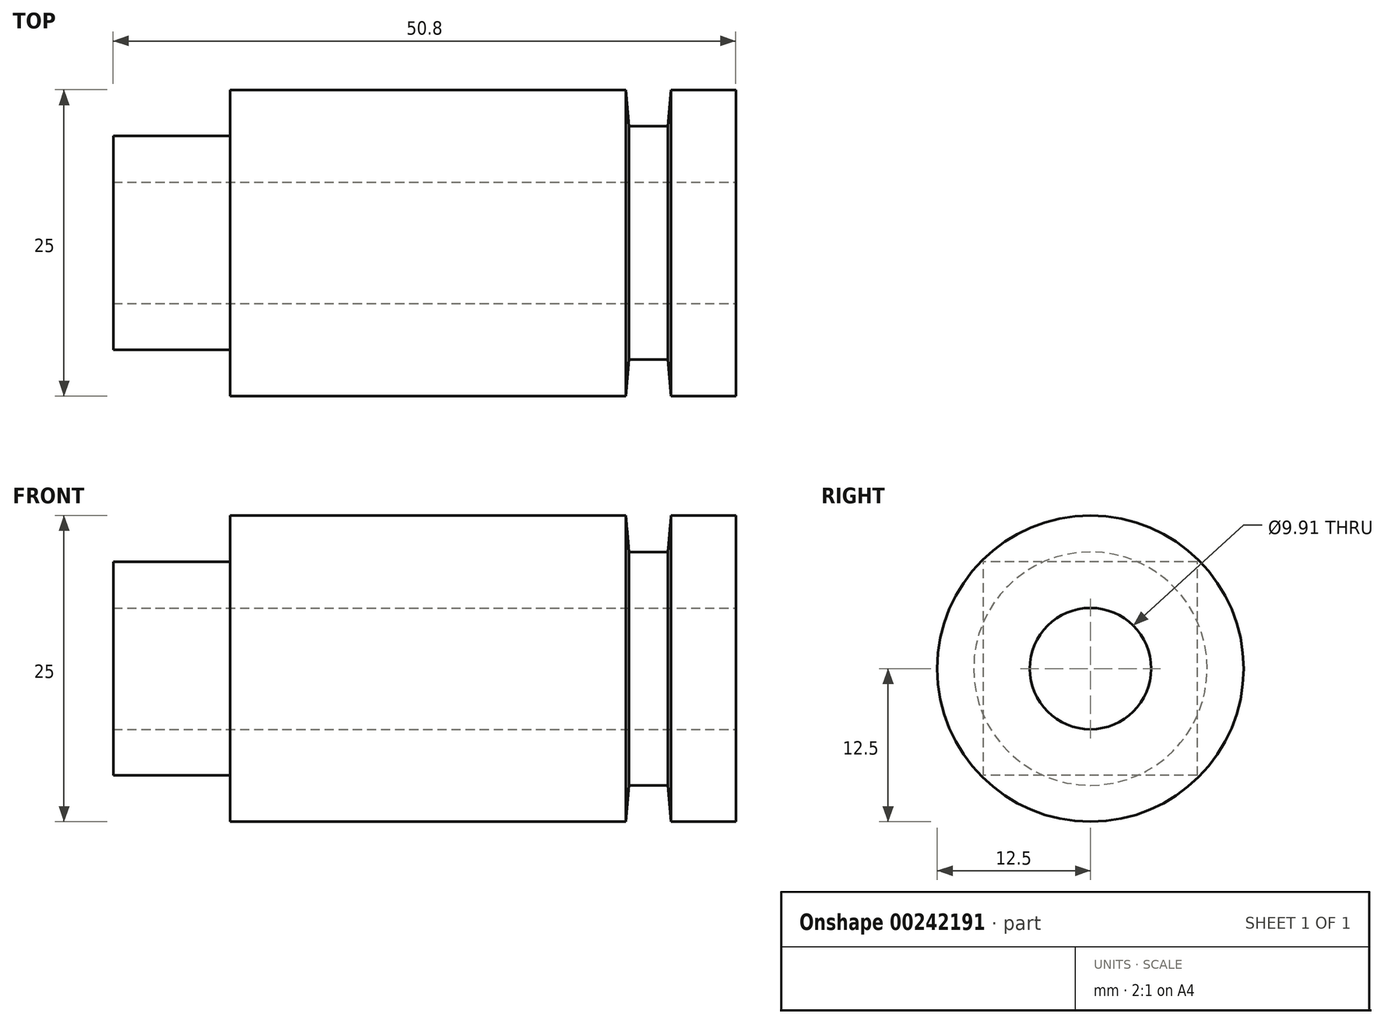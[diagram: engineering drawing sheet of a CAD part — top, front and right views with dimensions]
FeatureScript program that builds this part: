
annotation { "Feature Type Name" : "Feature", "Feature Type Description" : "" }
export const myFeature = defineFeature(function(context is Context, id is Id, definition is map)
    precondition{}
    {
        {
            var Q0;
            Q0=qCreatedBy(makeId("Front.planeOp"),FACE);
            var sketch = newSketch(context, id + "F0", { "sketchPlane" : qUnion([Q0])});
            skLineSegment(sketch, "E0", {"start": v(-22.01, 7.53) * mm, "end": v(-22.01, 12.5) * mm});
            skLineSegment(sketch, "E1", {"start": v(-22.01, 12.5) * mm, "end": v(10.3, 12.5) * mm});
            skLineSegment(sketch, "E2", {"start": v(10.3, 12.5) * mm, "end": v(10.55, 9.52) * mm});
            skLineSegment(sketch, "E3", {"start": v(10.55, 9.52) * mm, "end": v(13.73, 9.52) * mm});
            skLineSegment(sketch, "E4", {"start": v(13.73, 9.52) * mm, "end": v(13.98, 12.5) * mm});
            skLineSegment(sketch, "E5", {"start": v(13.98, 12.5) * mm, "end": v(19.26, 12.5) * mm});
            skLineSegment(sketch, "E6", {"start": v(19.26, 12.5) * mm, "end": v(19.26, 3.8) * mm});
            skLineSegment(sketch, "E7", {"start": v(-22.01, 7.53) * mm, "end": v(-22.01, 0) * mm});
            skLineSegment(sketch, "E8", {"start": v(-22.01, 0) * mm, "end": v(19.26, 0) * mm});
            skLineSegment(sketch, "E9", {"start": v(19.26, 0) * mm, "end": v(19.26, 3.8) * mm});
            skSolve(sketch);
        }
        {
            var Q0;
            Q0 = qSketchRegion(id + "F0", true);
            var Q1;
            Q1 = qSketchRegion(id + "F2", true);
            var Q2;
            Q2=sQuery(id+"F0.wireOp",EDGE,"E8");
            revolve(context, id + "F1", {"entities" : qUnion([Q0, Q1]), "axis" : qUnion([Q2]), "revolveType" : RevolveType.FULL});
        }
        {
            var Q0;
            Q0=makeQuery(id+"F1.opRevolve","SWEPT_FACE",FACE,{"disambiguationData":[OSD([sQuery(id+"F0.wireOp",EDGE,"E0"),sQuery(id+"F0.wireOp",EDGE,"E7")])]});
            var sketch = newSketch(context, id + "F2", { "sketchPlane" : qUnion([Q0])});
            skLineSegment(sketch, "E10.bottom", {"start": v(-8.72, -8.72) * mm, "end": v(8.72, -8.72) * mm});
            skLineSegment(sketch, "E10.top", {"start": v(-8.72, 8.72) * mm, "end": v(8.72, 8.72) * mm});
            skLineSegment(sketch, "E10.left", {"start": v(-8.72, -8.72) * mm, "end": v(-8.72, 8.72) * mm});
            skLineSegment(sketch, "E10.right", {"start": v(8.72, -8.72) * mm, "end": v(8.72, 8.72) * mm});
            skSolve(sketch);
        }
        {
            var Q0;
            {var subQ0=sQuery(id+"F2.wireOp",EDGE,"E10.left");var subQ1=sQuery(id+"F2.wireOp",EDGE,"E10.top");var subQ2=makeQuery(id+"F2.imprint","INTERSECT",VERTEX,{"derivedFrom":[subQ1,subQ0]});Q0=makeQuery(id+"F2.imprint","IMPRINT",FACE,{"disambiguationData":[TD([[makeQuery(id+"F2.imprint","IMPRINT",EDGE,{"disambiguationData":[TD([[subQ2,-1.0]])],"derivedFrom":subQ1}),-1.0]])]});}
            var Q1;
            {var subQ2=sQuery(id+"F2.wireOp",EDGE,"E10.bottom");Q1=makeQuery(id+"F2.imprint","IMPRINT",FACE,{"disambiguationData":[TD([[makeQuery(id+"F2.imprint","IMPRINT",EDGE,{"derivedFrom":subQ2}),1.0]])]});}
            extrude(context, id + "F3", {"entities" : qUnion([Q0, Q1]), "operationType" : NewBodyOperationType.ADD, "depth" : 9.52 * mm});
        }
        {
            var Q0;
            Q0=makeQuery(id+"F1.opRevolve","SWEPT_FACE",FACE,{"disambiguationData":[OSD([sQuery(id+"F0.wireOp",EDGE,"E6"),sQuery(id+"F0.wireOp",EDGE,"E9")])]});
            var sketch = newSketch(context, id + "F4", { "sketchPlane" : qUnion([Q0])});
            skCircle(sketch, "E11", {"center": v(0, 0) * mm, "radius": 4.95 * mm});
            skSolve(sketch);
        }
        {
            var Q0;
            Q0=makeQuery(id+"F4.imprint","IMPRINT",FACE,{"disambiguationData":[TD([[makeQuery(id+"F4.imprint","IMPRINT",EDGE,{"derivedFrom":sQuery(id+"F4.wireOp",EDGE,"E11")}),1.0]])]});
            extrude(context, id + "F5", {"entities" : qUnion([Q0]), "operationType" : NewBodyOperationType.REMOVE, "oppositeDirection" : true, "depth" : 50.8 * mm});
        }
    });
